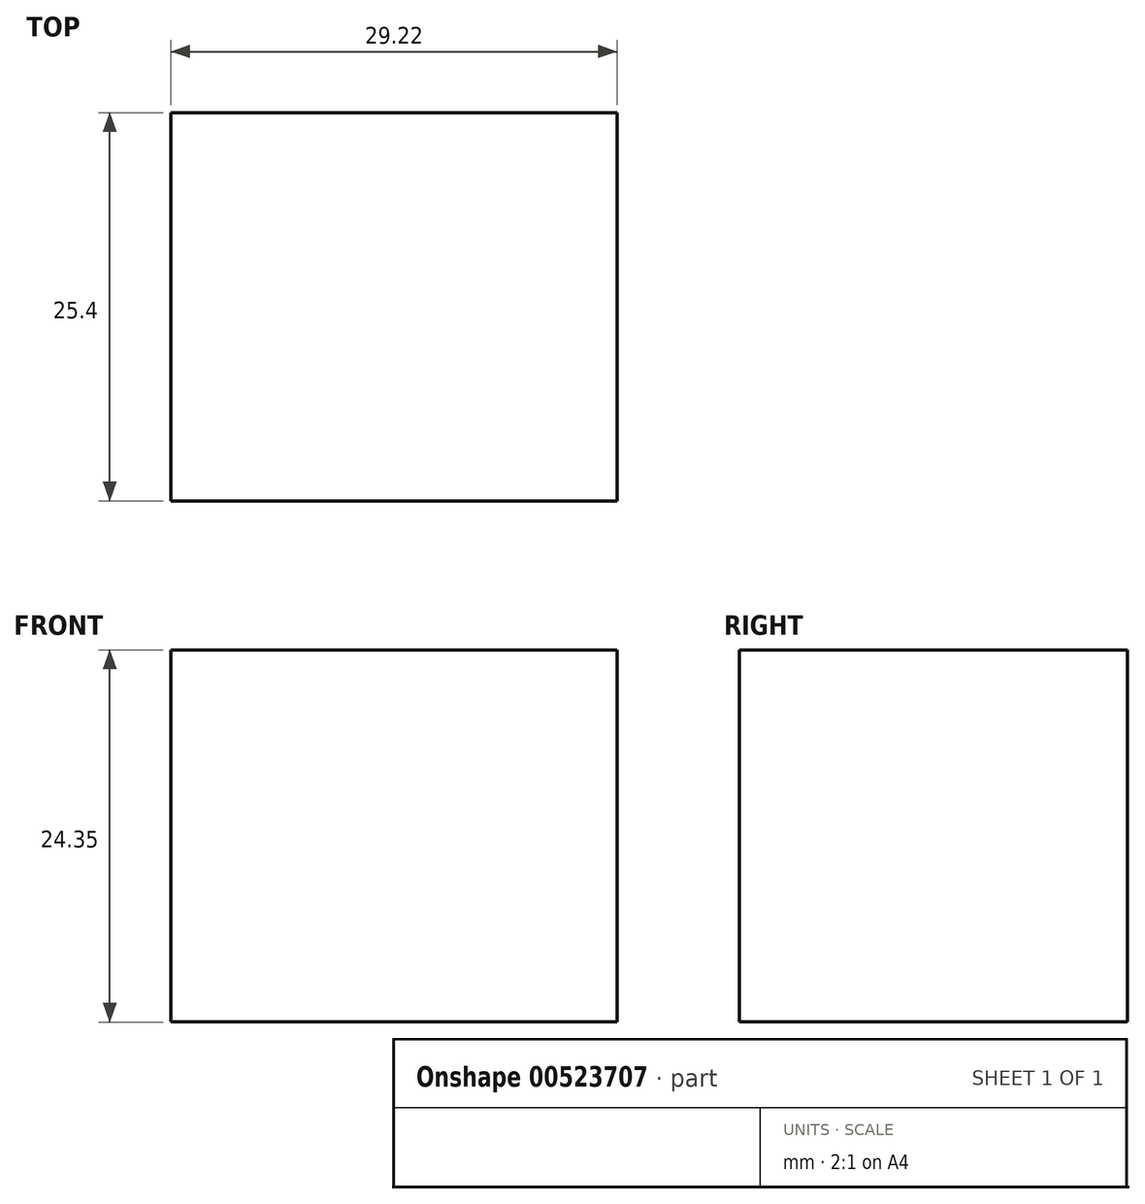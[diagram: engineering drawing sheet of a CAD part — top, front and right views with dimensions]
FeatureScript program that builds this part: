
annotation { "Feature Type Name" : "Feature", "Feature Type Description" : "" }
export const myFeature = defineFeature(function(context is Context, id is Id, definition is map)
    precondition{}
    {
        {
            var Q0;
            Q0=qCreatedBy(makeId("Front.planeOp"),FACE);
            var sketch = newSketch(context, id + "F0", { "sketchPlane" : qUnion([Q0])});
            skLineSegment(sketch, "E0.bottom", {"start": v(-46.6, 51.68) * mm, "end": v(-17.37, 51.68) * mm});
            skLineSegment(sketch, "E0.top", {"start": v(-46.6, 27.33) * mm, "end": v(-17.37, 27.33) * mm});
            skLineSegment(sketch, "E0.left", {"start": v(-46.6, 51.68) * mm, "end": v(-46.6, 27.33) * mm});
            skLineSegment(sketch, "E0.right", {"start": v(-17.37, 51.68) * mm, "end": v(-17.37, 27.33) * mm});
            skSolve(sketch);
        }
        {
            var Q0;
            Q0 = qSketchRegion(id + "F0", true);
            extrude(context, id + "F1", {"entities" : qUnion([Q0]), "depth" : 25.4 * mm, "offsetDistance" : 25.4 * mm});
        }
    });
